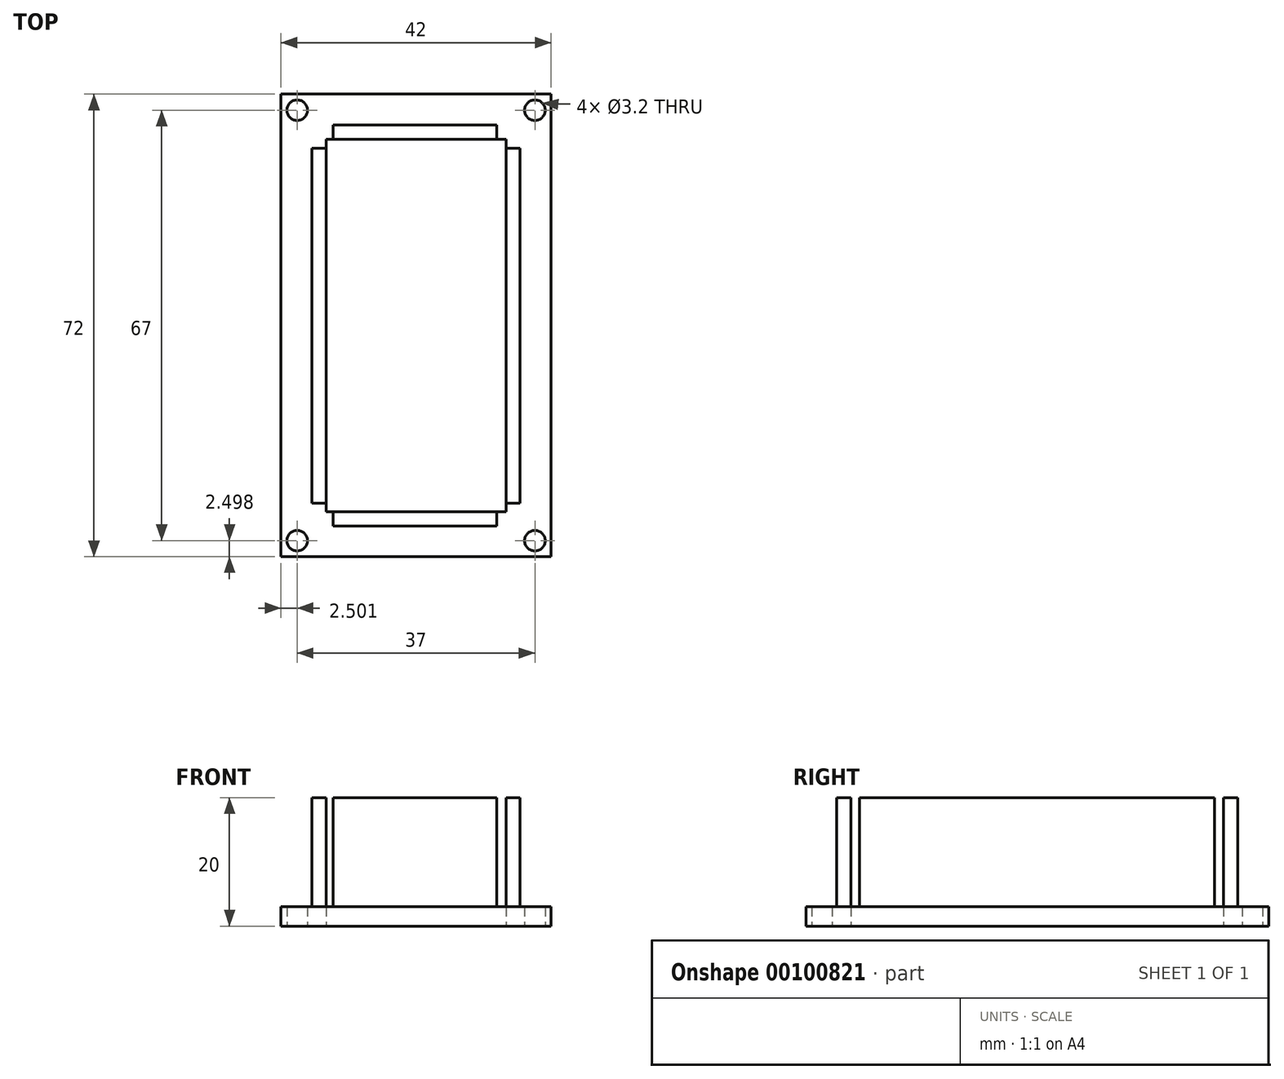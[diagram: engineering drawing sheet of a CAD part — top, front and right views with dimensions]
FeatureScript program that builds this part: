
annotation { "Feature Type Name" : "Feature", "Feature Type Description" : "" }
export const myFeature = defineFeature(function(context is Context, id is Id, definition is map)
    precondition{}
    {
        {
            var Q0;
            Q0=qCreatedBy(makeId("Top.planeOp"),FACE);
            var sketch = newSketch(context, id + "F0", { "sketchPlane" : qUnion([Q0])});
            skLineSegment(sketch, "E0.bottom", {"start": v(-23.09, 37.72) * mm, "end": v(18.91, 37.72) * mm});
            skLineSegment(sketch, "E0.top", {"start": v(-23.09, -34.28) * mm, "end": v(18.91, -34.28) * mm});
            skLineSegment(sketch, "E0.left", {"start": v(-23.09, 37.72) * mm, "end": v(-23.09, -34.28) * mm});
            skLineSegment(sketch, "E0.right", {"start": v(18.91, 37.72) * mm, "end": v(18.91, -34.28) * mm});
            skLineSegment(sketch, "E1.bottom", {"start": v(-16.09, 30.72) * mm, "end": v(11.91, 30.72) * mm});
            skLineSegment(sketch, "E1.top", {"start": v(-16.09, -27.28) * mm, "end": v(11.91, -27.28) * mm});
            skLineSegment(sketch, "E1.left", {"start": v(-16.09, 30.72) * mm, "end": v(-16.09, -27.28) * mm});
            skLineSegment(sketch, "E1.right", {"start": v(11.91, 30.72) * mm, "end": v(11.91, -27.28) * mm});
            skLineSegment(sketch, "E2", {"start": v(-2.09, 37.72) * mm, "end": v(-2.09, -34.28) * mm, "construction": true});
            skLineSegment(sketch, "E3", {"start": v(-23.09, 1.72) * mm, "end": v(18.91, 1.72) * mm, "construction": true});
            skPoint(sketch, "E4", {"position": v(11.91, 1.72) * mm});
            skPoint(sketch, "E5", {"position": v(-2.09, 30.72) * mm});
            skCircle(sketch, "E6", {"center": v(-20.59, 35.22) * mm, "radius": 1.6 * mm});
            skLineSegment(sketch, "E7.0", {"start": v(-18.29, 32.92) * mm, "end": v(14.11, 32.92) * mm});
            skLineSegment(sketch, "E7.1", {"start": v(-18.29, 32.92) * mm, "end": v(-18.29, -29.48) * mm});
            skLineSegment(sketch, "E7.2", {"start": v(-18.29, -29.48) * mm, "end": v(14.11, -29.48) * mm});
            skLineSegment(sketch, "E7.3", {"start": v(14.11, 32.92) * mm, "end": v(14.11, -29.48) * mm});
            skCircle(sketch, "E8", {"center": v(16.41, 35.22) * mm, "radius": 1.6 * mm});
            skCircle(sketch, "E9", {"center": v(-20.59, -31.78) * mm, "radius": 1.6 * mm});
            skCircle(sketch, "E10", {"center": v(16.41, -31.78) * mm, "radius": 1.6 * mm});
            skLineSegment(sketch, "E11", {"start": v(-20.59, 35.22) * mm, "end": v(-23.09, 35.22) * mm, "construction": true});
            skLineSegment(sketch, "E12", {"start": v(-20.59, 35.22) * mm, "end": v(-20.59, 37.72) * mm, "construction": true});
            skLineSegment(sketch, "E13", {"start": v(16.41, 37.72) * mm, "end": v(16.41, 35.22) * mm, "construction": true});
            skLineSegment(sketch, "E14", {"start": v(18.91, 35.22) * mm, "end": v(16.41, 35.22) * mm, "construction": true});
            skLineSegment(sketch, "E15", {"start": v(18.91, -31.78) * mm, "end": v(16.41, -31.78) * mm, "construction": true});
            skLineSegment(sketch, "E16", {"start": v(16.41, -31.78) * mm, "end": v(16.41, -34.28) * mm, "construction": true});
            skLineSegment(sketch, "E17", {"start": v(-20.59, -31.78) * mm, "end": v(-23.09, -31.78) * mm, "construction": true});
            skLineSegment(sketch, "E18", {"start": v(-20.59, -31.78) * mm, "end": v(-20.59, -34.28) * mm, "construction": true});
            skLineSegment(sketch, "E19", {"start": v(14.11, -27.28) * mm, "end": v(14.12, -27.4) * mm});
            skLineSegment(sketch, "E20", {"start": v(-15, -27.28) * mm, "end": v(-15, -29.48) * mm});
            skLineSegment(sketch, "E21", {"start": v(-16.09, -25.98) * mm, "end": v(-18.29, -25.98) * mm});
            skLineSegment(sketch, "E22", {"start": v(11.91, -25.98) * mm, "end": v(14.11, -25.98) * mm});
            skLineSegment(sketch, "E23", {"start": v(10.5, -27.28) * mm, "end": v(10.5, -29.48) * mm});
            skLineSegment(sketch, "E24", {"start": v(10.5, 30.72) * mm, "end": v(10.5, 32.92) * mm});
            skLineSegment(sketch, "E25", {"start": v(11.91, 29.3) * mm, "end": v(14.11, 29.3) * mm});
            skLineSegment(sketch, "E26", {"start": v(-16.09, 29.3) * mm, "end": v(-18.29, 29.3) * mm});
            skLineSegment(sketch, "E27", {"start": v(-15, 30.72) * mm, "end": v(-15, 32.92) * mm});
            skSolve(sketch);
        }
        {
            var Q0;
            Q0=makeQuery(id+"F0.imprint","IMPRINT",FACE,{"disambiguationData":[TD([[makeQuery(id+"F0.imprint","IMPRINT",EDGE,{"derivedFrom":sQuery(id+"F0.wireOp",EDGE,"E0.bottom")}),-1.0]])]});
            var Q1;
            {var subQ3=sQuery(id+"F0.wireOp",EDGE,"E20");Q1=makeQuery(id+"F0.imprint","IMPRINT",FACE,{"disambiguationData":[TD([[makeQuery(id+"F0.imprint","IMPRINT",EDGE,{"derivedFrom":subQ3}),-1.0]])]});}
            var Q2;
            {var subQ7=sQuery(id+"F0.wireOp",EDGE,"E26");Q2=makeQuery(id+"F0.imprint","IMPRINT",FACE,{"disambiguationData":[TD([[makeQuery(id+"F0.imprint","IMPRINT",EDGE,{"derivedFrom":subQ7}),-1.0]])]});}
            var Q3;
            {var subQ7=sQuery(id+"F0.wireOp",EDGE,"E24");Q3=makeQuery(id+"F0.imprint","IMPRINT",FACE,{"disambiguationData":[TD([[makeQuery(id+"F0.imprint","IMPRINT",EDGE,{"derivedFrom":subQ7}),-1.0]])]});}
            var Q4;
            {var subQ2=sQuery(id+"F0.wireOp",EDGE,"E22");Q4=makeQuery(id+"F0.imprint","IMPRINT",FACE,{"disambiguationData":[TD([[makeQuery(id+"F0.imprint","IMPRINT",EDGE,{"derivedFrom":subQ2}),-1.0]])]});}
            extrude(context, id + "F1", {"entities" : qUnion([Q0, Q1, Q2, Q3, Q4]), "depth" : 3 * mm});
        }
        {
            var Q0;
            {var subQ0=sQuery(id+"F0.wireOp",EDGE,"E24");Q0=makeQuery(id+"F0.imprint","IMPRINT",FACE,{"disambiguationData":[TD([[makeQuery(id+"F0.imprint","IMPRINT",EDGE,{"derivedFrom":subQ0}),1.0]])]});}
            var Q1;
            {var subQ0=sQuery(id+"F0.wireOp",EDGE,"E21");Q1=makeQuery(id+"F0.imprint","IMPRINT",FACE,{"disambiguationData":[TD([[makeQuery(id+"F0.imprint","IMPRINT",EDGE,{"derivedFrom":subQ0}),-1.0]])]});}
            var Q2;
            {var subQ0=sQuery(id+"F0.wireOp",EDGE,"E22");Q2=makeQuery(id+"F0.imprint","IMPRINT",FACE,{"disambiguationData":[TD([[makeQuery(id+"F0.imprint","IMPRINT",EDGE,{"derivedFrom":subQ0}),1.0]])]});}
            var Q3;
            {var subQ0=sQuery(id+"F0.wireOp",EDGE,"E20");Q3=makeQuery(id+"F0.imprint","IMPRINT",FACE,{"disambiguationData":[TD([[makeQuery(id+"F0.imprint","IMPRINT",EDGE,{"derivedFrom":subQ0}),1.0]])]});}
            extrude(context, id + "F2", {"entities" : qUnion([Q0, Q1, Q2, Q3]), "operationType" : NewBodyOperationType.ADD, "depth" : 20 * mm});
        }
    });
